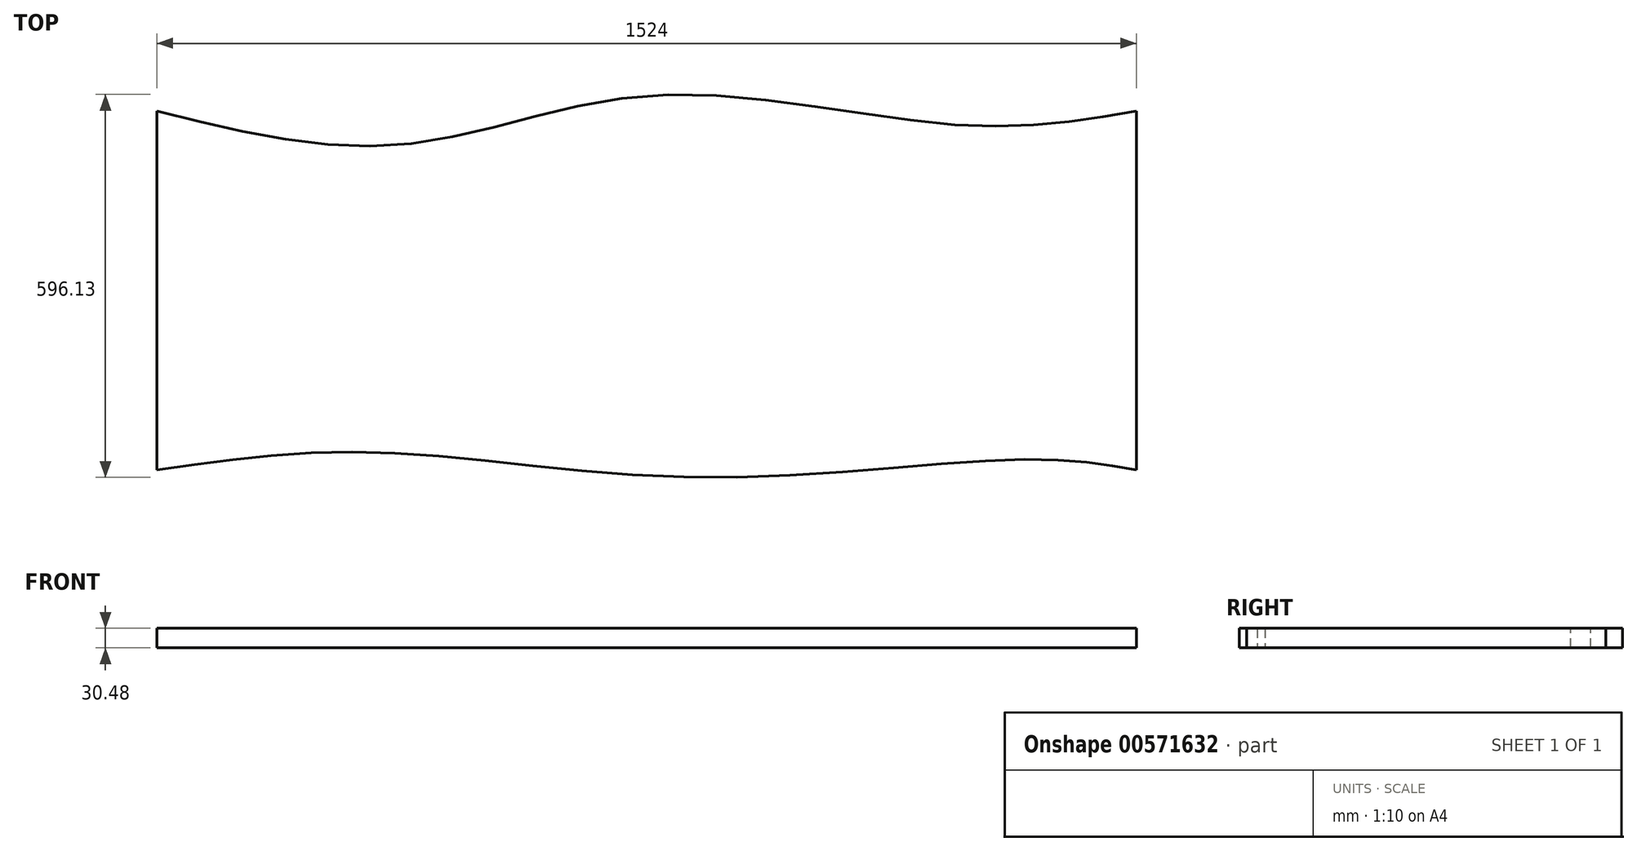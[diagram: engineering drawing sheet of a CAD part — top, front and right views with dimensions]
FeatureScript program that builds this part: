
annotation { "Feature Type Name" : "Feature", "Feature Type Description" : "" }
export const myFeature = defineFeature(function(context is Context, id is Id, definition is map)
    precondition{}
    {
        {
            var Q0;
            Q0=qCreatedBy(makeId("Top.planeOp"),FACE);
            var sketch = newSketch(context, id + "F0", { "sketchPlane" : qUnion([Q0])});
            skLineSegment(sketch, "E0.left", {"start": v(0, 0) * mm, "end": v(0, 558.8) * mm});
            skLineSegment(sketch, "E0.right", {"start": v(1524, 0) * mm, "end": v(1524, 558.8) * mm});
            skFitSpline(sketch, "E1", {"points": [v(0, 558.8) * mm, v(381.9, 506.47) * mm, v(768.51, 583.24) * mm, v(1247.25, 537.18) * mm, v(1524, 558.8) * mm], "startDerivative": vector(1538.73, -380.56) * mm, "endDerivative": vector(1189.38, 202.4) * mm});
            skFitSpline(sketch, "E2", {"points": [v(0, 0) * mm, v(338.63, 27.74) * mm, v(843.88, -11.34) * mm, v(1354.72, 16.57) * mm, v(1524, 0) * mm], "startDerivative": vector(1347.5, 194.65) * mm, "endDerivative": vector(851.25, -151.6) * mm});
            skSolve(sketch);
        }
        {
            var Q0;
            Q0 = qSketchRegion(id + "F0", true);
            extrude(context, id + "F1", {"entities" : qUnion([Q0]), "depth" : 30.48 * mm, "offsetDistance" : 25.4 * mm});
        }
    });
